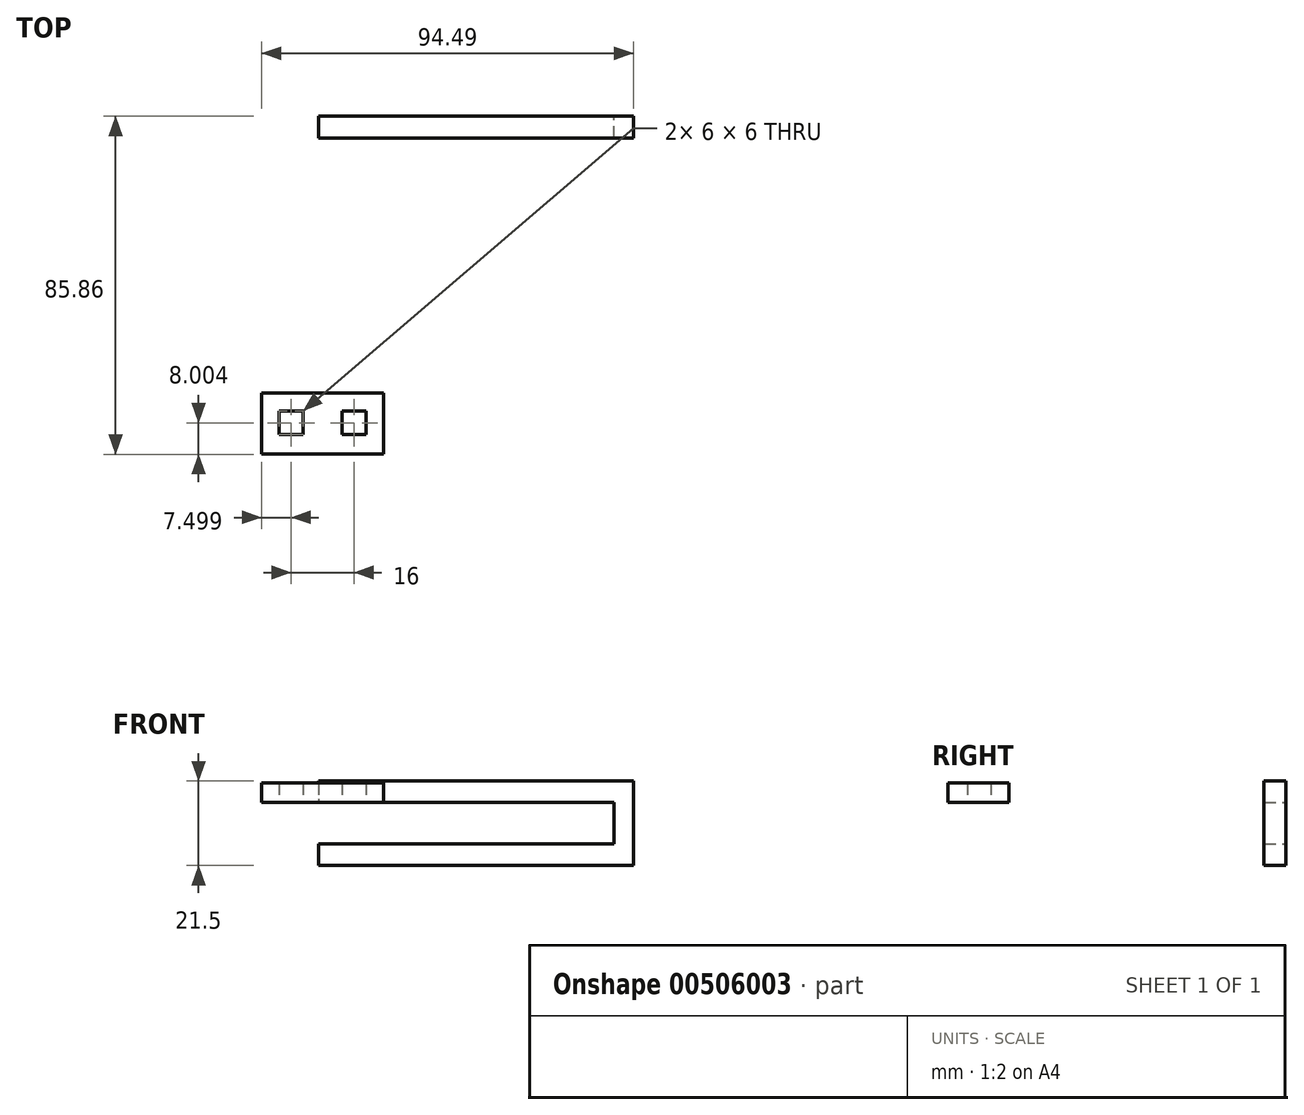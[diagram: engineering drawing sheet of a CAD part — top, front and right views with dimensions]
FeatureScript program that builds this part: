
annotation { "Feature Type Name" : "Feature", "Feature Type Description" : "" }
export const myFeature = defineFeature(function(context is Context, id is Id, definition is map)
    precondition{}
    {
        {
            var Q0;
            Q0=qCreatedBy(makeId("Top.planeOp"),FACE);
            var sketch = newSketch(context, id + "F0", { "sketchPlane" : qUnion([Q0])});
            skLineSegment(sketch, "E0.bottom", {"start": v(0, 0) * mm, "end": v(80, 0) * mm});
            skLineSegment(sketch, "E0.top", {"start": v(0, 5.5) * mm, "end": v(80, 5.5) * mm});
            skLineSegment(sketch, "E0.left", {"start": v(0, 0) * mm, "end": v(0, 5.5) * mm});
            skLineSegment(sketch, "E0.right", {"start": v(80, 0) * mm, "end": v(80, 5.5) * mm});
            skSolve(sketch);
        }
        {
            var Q0;
            Q0 = qSketchRegion(id + "F0", true);
            extrude(context, id + "F1", {"entities" : qUnion([Q0]), "depth" : 5.5 * mm});
        }
        {
            var Q0;
            Q0=makeQuery(id+"F1.opExtrude","CAP_FACE",FACE,{"disambiguationData":[OSD([sQuery(id+"F0.wireOp",EDGE,"E0.bottom"),sQuery(id+"F0.wireOp",EDGE,"E0.top"),sQuery(id+"F0.wireOp",EDGE,"E0.left"),sQuery(id+"F0.wireOp",EDGE,"E0.right")])],"isStart":true});
            var sketch = newSketch(context, id + "F2", { "sketchPlane" : qUnion([Q0])});
            skLineSegment(sketch, "E1.bottom", {"start": v(80, 0) * mm, "end": v(75, 0) * mm});
            skLineSegment(sketch, "E1.top", {"start": v(80, -5.5) * mm, "end": v(75, -5.5) * mm});
            skLineSegment(sketch, "E1.left", {"start": v(80, 0) * mm, "end": v(80, -5.5) * mm});
            skLineSegment(sketch, "E1.right", {"start": v(75, 0) * mm, "end": v(75, -5.5) * mm});
            skSolve(sketch);
        }
        {
            var Q0;
            Q0 = qSketchRegion(id + "F2", true);
            extrude(context, id + "F3", {"entities" : qUnion([Q0]), "operationType" : NewBodyOperationType.ADD, "depth" : 16 * mm});
        }
        {
            var Q0;
            Q0=makeQuery(id+"F3.opExtrude","SWEPT_FACE",FACE,{"disambiguationData":[OSD([sQuery(id+"F2.wireOp",EDGE,"E1.right")])]});
            var sketch = newSketch(context, id + "F4", { "sketchPlane" : qUnion([Q0])});
            skLineSegment(sketch, "E2.bottom", {"start": v(0, -16) * mm, "end": v(-5.5, -16) * mm});
            skLineSegment(sketch, "E2.top", {"start": v(0, -10.5) * mm, "end": v(-5.5, -10.5) * mm});
            skLineSegment(sketch, "E2.left", {"start": v(0, -16) * mm, "end": v(0, -10.5) * mm});
            skLineSegment(sketch, "E2.right", {"start": v(-5.5, -16) * mm, "end": v(-5.5, -10.5) * mm});
            skSolve(sketch);
        }
        {
            var Q0;
            Q0=makeQuery(id+"F4.imprint","IMPRINT",FACE,{"disambiguationData":[TD([[makeQuery(id+"F4.imprint","IMPRINT",EDGE,{"derivedFrom":sQuery(id+"F4.wireOp",EDGE,"E2.bottom")}),-1.0]])]});
            extrude(context, id + "F5", {"entities" : qUnion([Q0]), "operationType" : NewBodyOperationType.ADD, "depth" : 75 * mm});
        }
        {
            var Q0;
            Q0=qCreatedBy(makeId("Top.planeOp"),FACE);
            var sketch = newSketch(context, id + "F6", { "sketchPlane" : qUnion([Q0])});
            skLineSegment(sketch, "E3.bottom", {"start": v(16.5, -64.86) * mm, "end": v(-14.5, -64.86) * mm});
            skLineSegment(sketch, "E3.top", {"start": v(16.5, -80.36) * mm, "end": v(-14.5, -80.36) * mm});
            skLineSegment(sketch, "E3.left", {"start": v(16.5, -64.86) * mm, "end": v(16.5, -80.36) * mm});
            skLineSegment(sketch, "E3.right", {"start": v(-14.5, -64.86) * mm, "end": v(-14.5, -80.36) * mm});
            skLineSegment(sketch, "E4.bottom", {"start": v(6, -75.36) * mm, "end": v(12, -75.36) * mm});
            skLineSegment(sketch, "E4.top", {"start": v(6, -69.36) * mm, "end": v(12, -69.36) * mm});
            skLineSegment(sketch, "E4.left", {"start": v(6, -75.36) * mm, "end": v(6, -69.36) * mm});
            skLineSegment(sketch, "E4.right", {"start": v(12, -75.36) * mm, "end": v(12, -69.36) * mm});
            skPoint(sketch, "E4.middle", {"position": v(9, -72.36) * mm});
            skLineSegment(sketch, "E5", {"start": v(1, -64.86) * mm, "end": v(1, -69.25) * mm});
            skLineSegment(sketch, "E6.MirrorCS", {"start": v(-10, -75.36) * mm, "end": v(-10, -69.36) * mm});
            skLineSegment(sketch, "E7.MirrorCS", {"start": v(-4, -75.36) * mm, "end": v(-4, -69.36) * mm});
            skLineSegment(sketch, "E8.MirrorCS", {"start": v(-4, -75.36) * mm, "end": v(-10, -75.36) * mm});
            skLineSegment(sketch, "E9.MirrorCS", {"start": v(-4, -69.36) * mm, "end": v(-10, -69.36) * mm});
            skPoint(sketch, "E10.MirrorP", {"position": v(-7, -72.36) * mm});
            skSolve(sketch);
        }
        {
            var Q0;
            Q0 = qSketchRegion(id + "F6", true);
            extrude(context, id + "F7", {"entities" : qUnion([Q0]), "depth" : 5 * mm});
        }
    });
